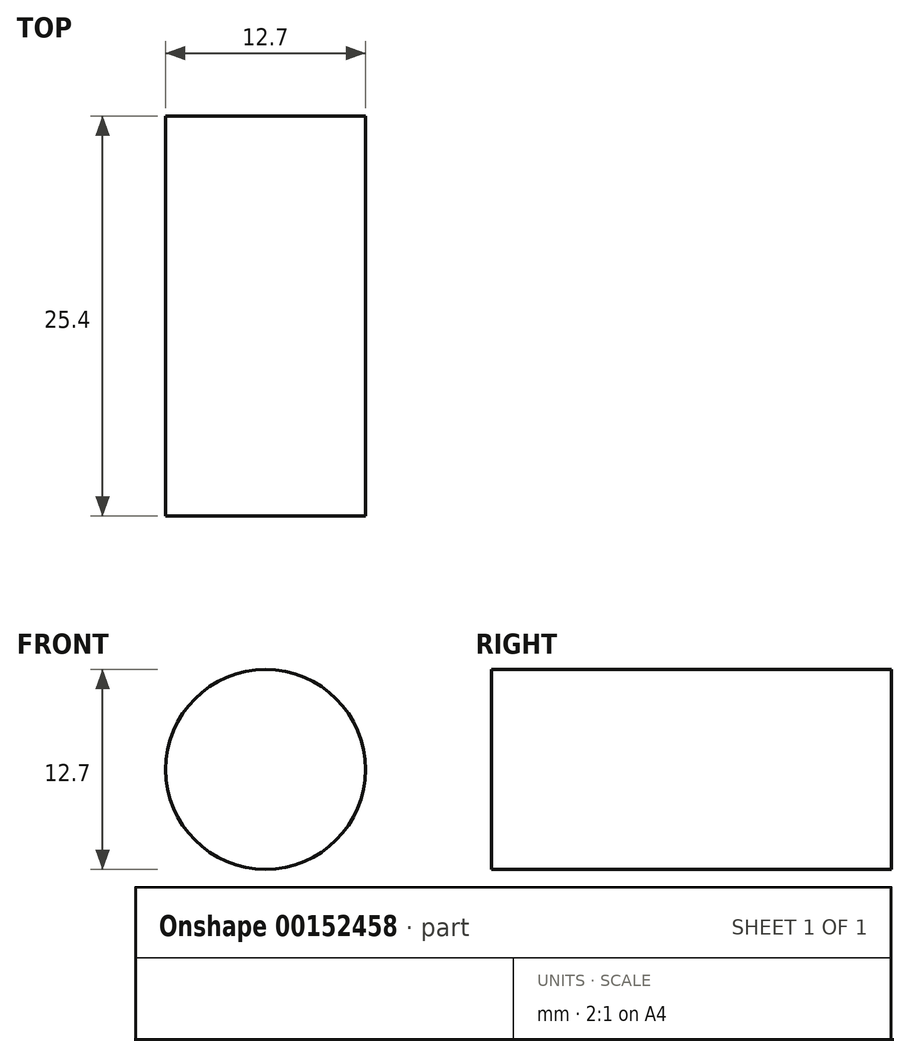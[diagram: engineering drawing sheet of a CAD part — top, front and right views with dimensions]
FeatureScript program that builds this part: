
annotation { "Feature Type Name" : "Feature", "Feature Type Description" : "" }
export const myFeature = defineFeature(function(context is Context, id is Id, definition is map)
    precondition{}
    {
        {
            var Q0;
            Q0=qCreatedBy(makeId("Front.planeOp"),FACE);
            var sketch = newSketch(context, id + "F0", { "sketchPlane" : qUnion([Q0])});
            skCircle(sketch, "E0", {"center": v(0, 0) * mm, "radius": 9.53 * mm});
            skCircle(sketch, "E1", {"center": v(0, 0) * mm, "radius": 6.35 * mm});
            skSolve(sketch);
        }
        {
            var Q0;
            Q0=makeQuery(id+"F0.imprint","IMPRINT",FACE,{"disambiguationData":[TD([[makeQuery(id+"F0.imprint","IMPRINT",EDGE,{"derivedFrom":sQuery(id+"F0.wireOp",EDGE,"E1")}),1.0]])]});
            var Q1;
            Q1=sQuery(id+"F0.wireOp",EDGE,"E1");
            extrude(context, id + "F1", {"entities" : qUnion([Q0]), "surfaceEntities" : qUnion([Q1]), "depth" : 25.4 * mm});
        }
    });
